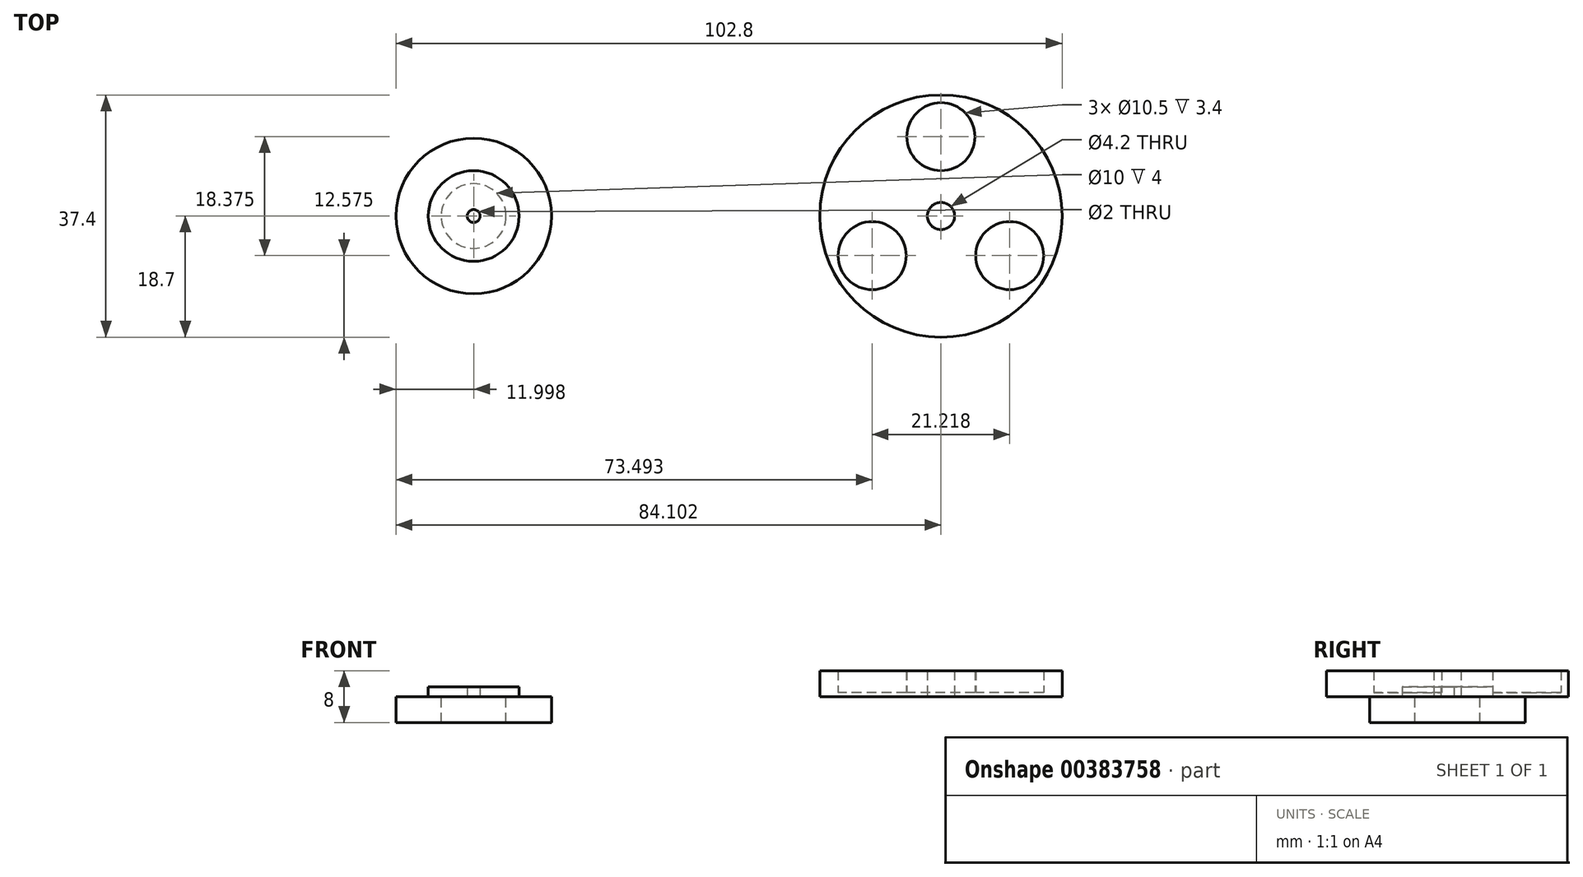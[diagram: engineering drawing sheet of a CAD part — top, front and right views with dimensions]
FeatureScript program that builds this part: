
annotation { "Feature Type Name" : "Feature", "Feature Type Description" : "" }
export const myFeature = defineFeature(function(context is Context, id is Id, definition is map)
    precondition{}
    {
        {
            var Q0;
            Q0=qCreatedBy(makeId("Top.planeOp"),FACE);
            var sketch = newSketch(context, id + "F0", { "sketchPlane" : qUnion([Q0])});
            skCircle(sketch, "E0", {"center": v(-42.8, 0) * mm, "radius": 5 * mm});
            skCircle(sketch, "E1", {"center": v(-42.8, 0) * mm, "radius": 12 * mm});
            skCircle(sketch, "E2", {"center": v(-42.8, 0) * mm, "radius": 4 * mm});
            skCircle(sketch, "E3", {"center": v(-42.8, 0) * mm, "radius": 1 * mm});
            skCircle(sketch, "E4", {"center": v(-42.8, 0) * mm, "radius": 7 * mm});
            skCircle(sketch, "E5", {"center": v(29.31, 0) * mm, "radius": 3.75 * mm});
            skCircle(sketch, "E6", {"center": v(29.31, 0) * mm, "radius": 12.25 * mm, "construction": true});
            skCircle(sketch, "E7", {"center": v(29.31, 12.25) * mm, "radius": 5.25 * mm});
            skCircle(sketch, "E8", {"center": v(29.31, 0) * mm, "radius": 18.7 * mm});
            skCircle(sketch, "E9.1.0", {"center": v(18.7, -6.12) * mm, "radius": 5.25 * mm});
            skCircle(sketch, "E9.2.0", {"center": v(39.92, -6.12) * mm, "radius": 5.25 * mm});
            skCircle(sketch, "E10", {"center": v(29.31, 0) * mm, "radius": 2.1 * mm});
            skCircle(sketch, "E11", {"center": v(29.31, 0) * mm, "radius": 7.5 * mm});
            skSolve(sketch);
        }
        {
            var Q0;
            Q0=makeQuery(id+"F0.imprint","IMPRINT",FACE,{"disambiguationData":[TD([[makeQuery(id+"F0.imprint","IMPRINT",EDGE,{"derivedFrom":sQuery(id+"F0.wireOp",EDGE,"E0")}),-1.0]])]});
            var Q1;
            Q1=makeQuery(id+"F0.imprint","IMPRINT",FACE,{"disambiguationData":[TD([[makeQuery(id+"F0.imprint","IMPRINT",EDGE,{"derivedFrom":sQuery(id+"F0.wireOp",EDGE,"E1")}),1.0]])]});
            extrude(context, id + "F1", {"entities" : qUnion([Q0, Q1]), "oppositeDirection" : true, "depth" : 4 * mm});
        }
        {
            var Q0;
            Q0=makeQuery(id+"F0.imprint","IMPRINT",FACE,{"disambiguationData":[TD([[makeQuery(id+"F0.imprint","IMPRINT",EDGE,{"derivedFrom":sQuery(id+"F0.wireOp",EDGE,"E0")}),-1.0]])]});
            var Q1;
            Q1=makeQuery(id+"F0.imprint","IMPRINT",FACE,{"disambiguationData":[TD([[makeQuery(id+"F0.imprint","IMPRINT",EDGE,{"derivedFrom":sQuery(id+"F0.wireOp",EDGE,"E0")}),1.0]])]});
            var Q2;
            Q2=makeQuery(id+"F0.imprint","IMPRINT",FACE,{"disambiguationData":[TD([[makeQuery(id+"F0.imprint","IMPRINT",EDGE,{"derivedFrom":sQuery(id+"F0.wireOp",EDGE,"E2")}),1.0]])]});
            extrude(context, id + "F2", {"entities" : qUnion([Q0, Q1, Q2]), "operationType" : NewBodyOperationType.ADD, "depth" : 1.5 * mm});
        }
        {
            var Q0;
            Q0=makeQuery(id+"F0.imprint","IMPRINT",FACE,{"disambiguationData":[TD([[makeQuery(id+"F0.imprint","IMPRINT",EDGE,{"derivedFrom":sQuery(id+"F0.wireOp",EDGE,"E5")}),-1.0]])]});
            var Q1;
            Q1=makeQuery(id+"F0.imprint","IMPRINT",FACE,{"disambiguationData":[TD([[makeQuery(id+"F0.imprint","IMPRINT",EDGE,{"derivedFrom":sQuery(id+"F0.wireOp",EDGE,"E9.1.0")}),1.0]])]});
            var Q2;
            Q2=makeQuery(id+"F0.imprint","IMPRINT",FACE,{"disambiguationData":[TD([[makeQuery(id+"F0.imprint","IMPRINT",EDGE,{"derivedFrom":sQuery(id+"F0.wireOp",EDGE,"E5")}),1.0]])]});
            var Q3;
            Q3=makeQuery(id+"F0.imprint","IMPRINT",FACE,{"disambiguationData":[TD([[makeQuery(id+"F0.imprint","IMPRINT",EDGE,{"derivedFrom":sQuery(id+"F0.wireOp",EDGE,"E7")}),1.0]])]});
            var Q4;
            Q4=makeQuery(id+"F0.imprint","IMPRINT",FACE,{"disambiguationData":[TD([[makeQuery(id+"F0.imprint","IMPRINT",EDGE,{"derivedFrom":sQuery(id+"F0.wireOp",EDGE,"E9.2.0")}),1.0]])]});
            var Q5;
            Q5=makeQuery(id+"F0.imprint","IMPRINT",FACE,{"disambiguationData":[TD([[makeQuery(id+"F0.imprint","IMPRINT",EDGE,{"derivedFrom":sQuery(id+"F0.wireOp",EDGE,"E8")}),1.0]])]});
            extrude(context, id + "F3", {"entities" : qUnion([Q0, Q1, Q2, Q3, Q4, Q5]), "depth" : 0.6 * mm, "offsetDistance" : 25 * mm});
        }
        {
            var Q0;
            Q0=makeQuery(id+"F0.imprint","IMPRINT",FACE,{"disambiguationData":[TD([[makeQuery(id+"F0.imprint","IMPRINT",EDGE,{"derivedFrom":sQuery(id+"F0.wireOp",EDGE,"E5")}),-1.0]])]});
            var Q1;
            Q1=makeQuery(id+"F0.imprint","IMPRINT",FACE,{"disambiguationData":[TD([[makeQuery(id+"F0.imprint","IMPRINT",EDGE,{"derivedFrom":sQuery(id+"F0.wireOp",EDGE,"E5")}),1.0]])]});
            var Q2;
            Q2=makeQuery(id+"F0.imprint","IMPRINT",FACE,{"disambiguationData":[TD([[makeQuery(id+"F0.imprint","IMPRINT",EDGE,{"derivedFrom":sQuery(id+"F0.wireOp",EDGE,"E8")}),1.0]])]});
            extrude(context, id + "F4", {"entities" : qUnion([Q0, Q1, Q2]), "operationType" : NewBodyOperationType.ADD, "depth" : 4 * mm, "offsetDistance" : 25 * mm});
        }
    });
